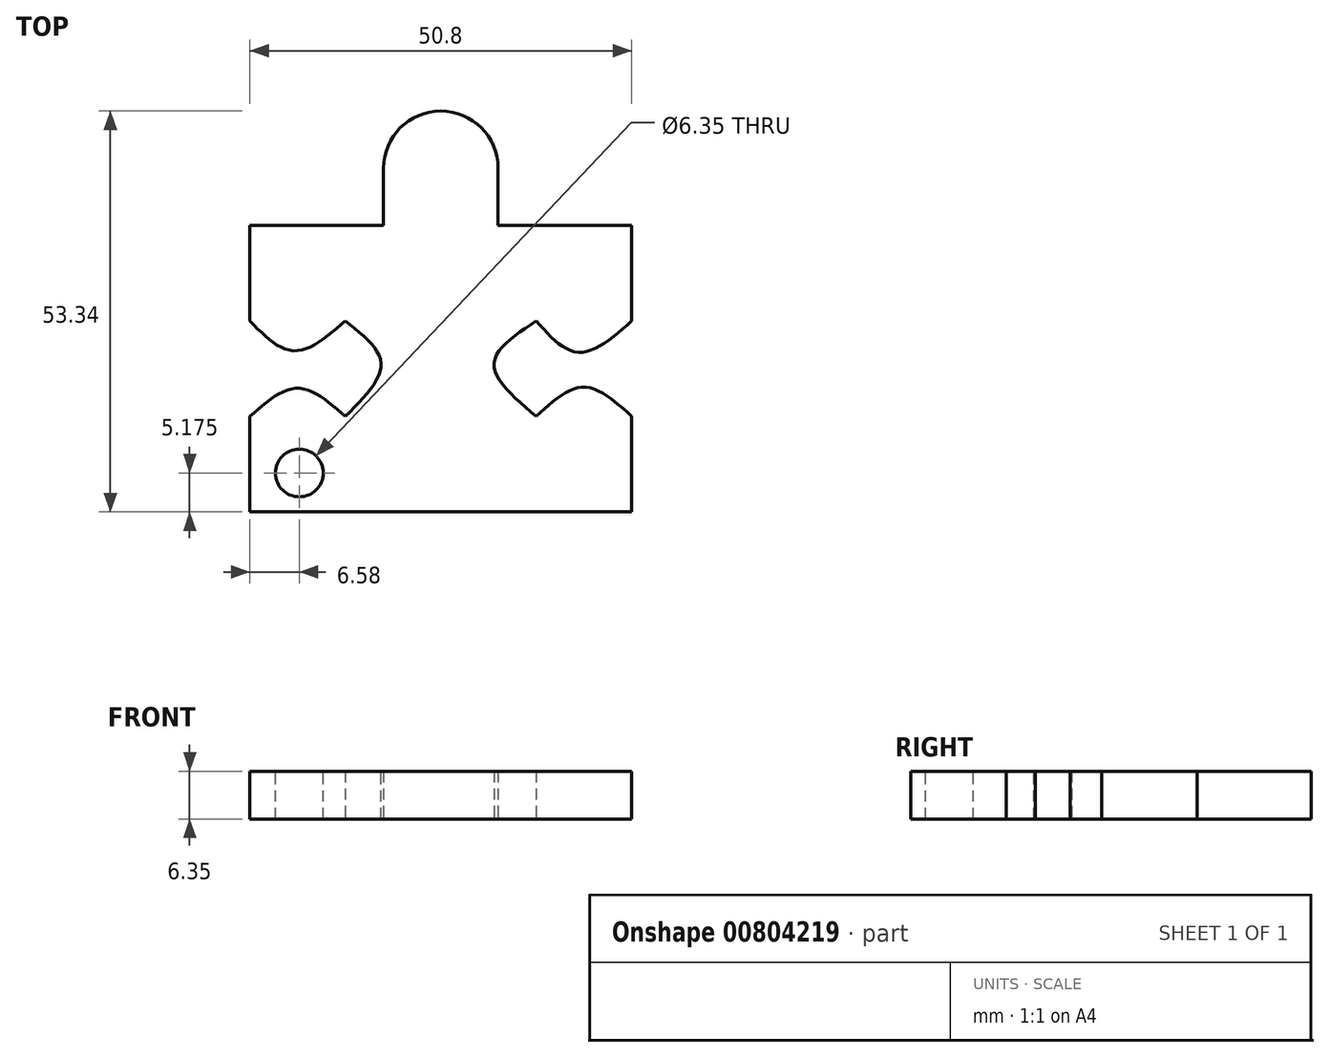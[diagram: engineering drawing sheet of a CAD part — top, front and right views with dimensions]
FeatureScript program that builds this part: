
annotation { "Feature Type Name" : "Feature", "Feature Type Description" : "" }
export const myFeature = defineFeature(function(context is Context, id is Id, definition is map)
    precondition{}
    {
        {
            var Q0;
            Q0=qCreatedBy(makeId("Top.planeOp"),FACE);
            var sketch = newSketch(context, id + "F0", { "sketchPlane" : qUnion([Q0])});
            skLineSegment(sketch, "E0", {"start": v(0, 0) * mm, "end": v(50.8, 0) * mm});
            skLineSegment(sketch, "E1", {"start": v(0, 0) * mm, "end": v(0, 12.7) * mm});
            skLineSegment(sketch, "E2", {"start": v(50.8, 0) * mm, "end": v(50.8, 12.7) * mm});
            skLineSegment(sketch, "E3", {"start": v(50.8, 25.4) * mm, "end": v(50.8, 38.1) * mm});
            skLineSegment(sketch, "E4", {"start": v(0, 25.4) * mm, "end": v(0, 38.1) * mm});
            skLineSegment(sketch, "E5", {"start": v(0, 38.1) * mm, "end": v(17.78, 38.1) * mm});
            skLineSegment(sketch, "E6", {"start": v(50.8, 38.1) * mm, "end": v(33.02, 38.1) * mm});
            skPoint(sketch, "E7.1.internal.snap0", {"position": v(6.35, 12.7) * mm});
            skFitSpline(sketch, "E7", {"points": [v(0, 12.7) * mm, v(6.35, 16.44) * mm, v(12.7, 12.7) * mm], "startDerivative": vector(12.7, 11.23) * mm, "endDerivative": vector(12.7, -11.23) * mm});
            skFitSpline(sketch, "E8", {"points": [v(50.8, 12.7) * mm, v(44.4, 16.6) * mm, v(38.1, 12.7) * mm], "startDerivative": vector(-12.8, 11.68) * mm, "endDerivative": vector(-12.6, -11.7) * mm});
            skFitSpline(sketch, "E9", {"points": [v(38.1, 12.7) * mm, v(32.49, 19.72) * mm, v(38.1, 25.4) * mm], "startDerivative": vector(-16.69, 14.13) * mm, "endDerivative": vector(17.02, 11.24) * mm});
            skFitSpline(sketch, "E10", {"points": [v(12.7, 12.7) * mm, v(17.45, 19.72) * mm, v(12.7, 25.4) * mm], "startDerivative": vector(14.1, 14.05) * mm, "endDerivative": vector(-14.42, 11.32) * mm});
            skFitSpline(sketch, "E11", {"points": [v(0, 25.4) * mm, v(5.9, 21.44) * mm, v(12.7, 25.4) * mm], "startDerivative": vector(11.82, -12) * mm, "endDerivative": vector(13.57, 11.8) * mm});
            skFitSpline(sketch, "E12", {"points": [v(38.1, 25.4) * mm, v(43.76, 21.23) * mm, v(50.8, 25.4) * mm], "startDerivative": vector(11.34, -12.69) * mm, "endDerivative": vector(14.03, 12.37) * mm});
            skLineSegment(sketch, "E13", {"start": v(17.78, 38.1) * mm, "end": v(17.78, 45.72) * mm});
            skLineSegment(sketch, "E14", {"start": v(33.02, 38.1) * mm, "end": v(33.02, 45.72) * mm});
            skArc(sketch, "E15", {"start": v(17.78, 45.72) * mm, "mid": v(25.4, 53.34) * mm, "end": v(33.02, 45.72) * mm});
            skSolve(sketch);
        }
        {
            var Q0;
            Q0=makeQuery(id+"F0.imprint","IMPRINT",FACE,{"disambiguationData":[TD([[makeQuery(id+"F0.imprint","IMPRINT",EDGE,{"derivedFrom":sQuery(id+"F0.wireOp",EDGE,"E0")}),1.0]])]});
            extrude(context, id + "F1", {"entities" : qUnion([Q0]), "depth" : 6.35 * mm, "offsetDistance" : 25.4 * mm});
        }
        {
            var Q0;
            Q0=makeQuery(id+"F1.opExtrude","CAP_FACE",FACE,{"disambiguationData":[OSD([sQuery(id+"F0.wireOp",EDGE,"E0"),sQuery(id+"F0.wireOp",EDGE,"E1"),sQuery(id+"F0.wireOp",EDGE,"E2"),sQuery(id+"F0.wireOp",EDGE,"E3"),sQuery(id+"F0.wireOp",EDGE,"E4"),sQuery(id+"F0.wireOp",EDGE,"E5"),sQuery(id+"F0.wireOp",EDGE,"E6"),sQuery(id+"F0.wireOp",EDGE,"E7"),sQuery(id+"F0.wireOp",EDGE,"E8"),sQuery(id+"F0.wireOp",EDGE,"E9"),sQuery(id+"F0.wireOp",EDGE,"E10"),sQuery(id+"F0.wireOp",EDGE,"E11"),sQuery(id+"F0.wireOp",EDGE,"E12"),sQuery(id+"F0.wireOp",EDGE,"E13"),sQuery(id+"F0.wireOp",EDGE,"E14"),sQuery(id+"F0.wireOp",EDGE,"E15")])],"isStart":false});
            var sketch = newSketch(context, id + "F2", { "sketchPlane" : qUnion([Q0])});
            skCircle(sketch, "E16", {"center": v(6.58, 5.17) * mm, "radius": 3.18 * mm});
            skSolve(sketch);
        }
        {
            var Q0;
            Q0 = qSketchRegion(id + "F2", true);
            extrude(context, id + "F3", {"entities" : qUnion([Q0]), "operationType" : NewBodyOperationType.REMOVE, "endBound" : BoundingType.UP_TO_NEXT, "oppositeDirection" : true, "depth" : 25.4 * mm, "offsetDistance" : 25.4 * mm});
        }
    });
